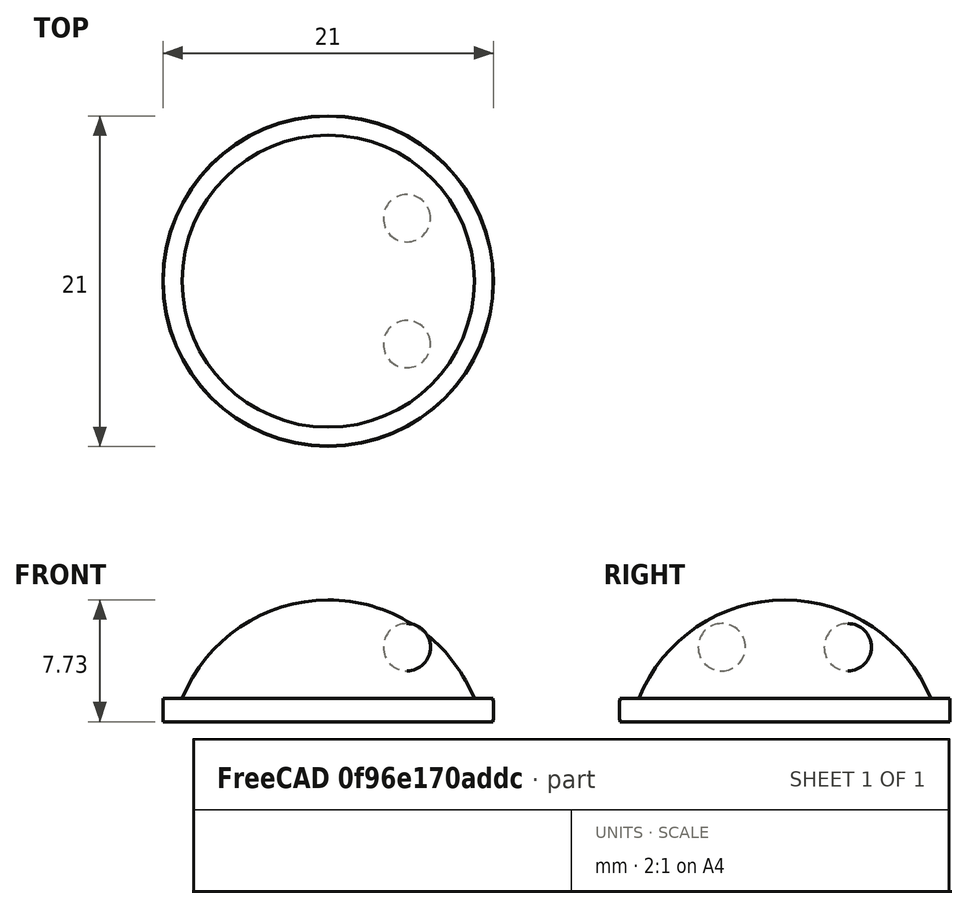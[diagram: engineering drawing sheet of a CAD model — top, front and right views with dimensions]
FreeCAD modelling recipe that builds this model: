
FCSTD DOCUMENT  (FreeCAD 0.21R33694 (Git))
Label: OJT1_T013R012_cap_robot
License: All rights reserved
LicenseURL: http://en.wikipedia.org/wiki/All_rights_reserved
objects: Part::Sphere×4, Part::MultiFuse×1
note: 5 computed .brp shape members not serialized (recipe doc carries the construction recipe); baked Part::Feature solids carry a one-line shape summary decoded from their .brp

FEATURE [Part::Sphere] Sphere
  Angle1 = 20
  Angle2 = 90
  Angle3 = 360
  AttacherType = Attacher::AttachEngine3D
  Placement = pos=(0,0,-3) rot=(0,0,1;0rad)
  Radius = 10
FEATURE [Part::Sphere] Sphere001  label="base"
  Angle1 = -4
  Angle2 = 4
  Angle3 = 360
  AttacherType = Attacher::AttachEngine3D
  Radius = 10.5
FEATURE [Part::MultiFuse] Fusion
  Refine = true
  Shapes = -> [Sphere,Sphere001]
FEATURE [Part::Sphere] Sphere002  label="ull1"
  Angle1 = -90
  Angle2 = 90
  Angle3 = 360
  AttacherType = Attacher::AttachEngine3D
  Placement = pos=(5,4,4) rot=(0,0,1;0rad)
  Radius = 1.5
FEATURE [Part::Sphere] Sphere003  label="ull2"
  Angle1 = -90
  Angle2 = 90
  Angle3 = 360
  AttacherType = Attacher::AttachEngine3D
  Placement = pos=(5,-4,4) rot=(0,0,1;0rad)
  Radius = 1.5
